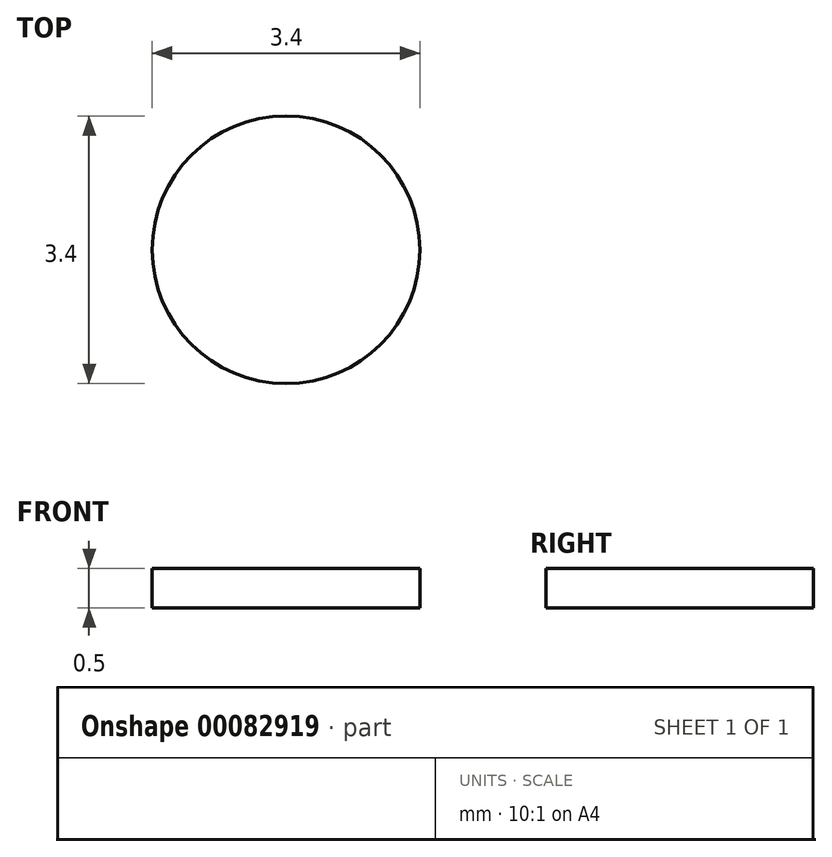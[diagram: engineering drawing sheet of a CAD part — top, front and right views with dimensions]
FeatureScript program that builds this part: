
annotation { "Feature Type Name" : "Feature", "Feature Type Description" : "" }
export const myFeature = defineFeature(function(context is Context, id is Id, definition is map)
    precondition{}
    {
        {
            var Q0;
            Q0=qCreatedBy(makeId("Top.planeOp"),FACE);
            var sketch = newSketch(context, id + "F0", { "sketchPlane" : qUnion([Q0])});
            skCircle(sketch, "E0", {"center": v(0, 0) * mm, "radius": 1.7 * mm});
            skSolve(sketch);
        }
        {
            var Q0;
            Q0 = qSketchRegion(id + "F0", true);
            extrude(context, id + "F1", {"entities" : qUnion([Q0]), "depth" : 0.5 * mm});
        }
    });
